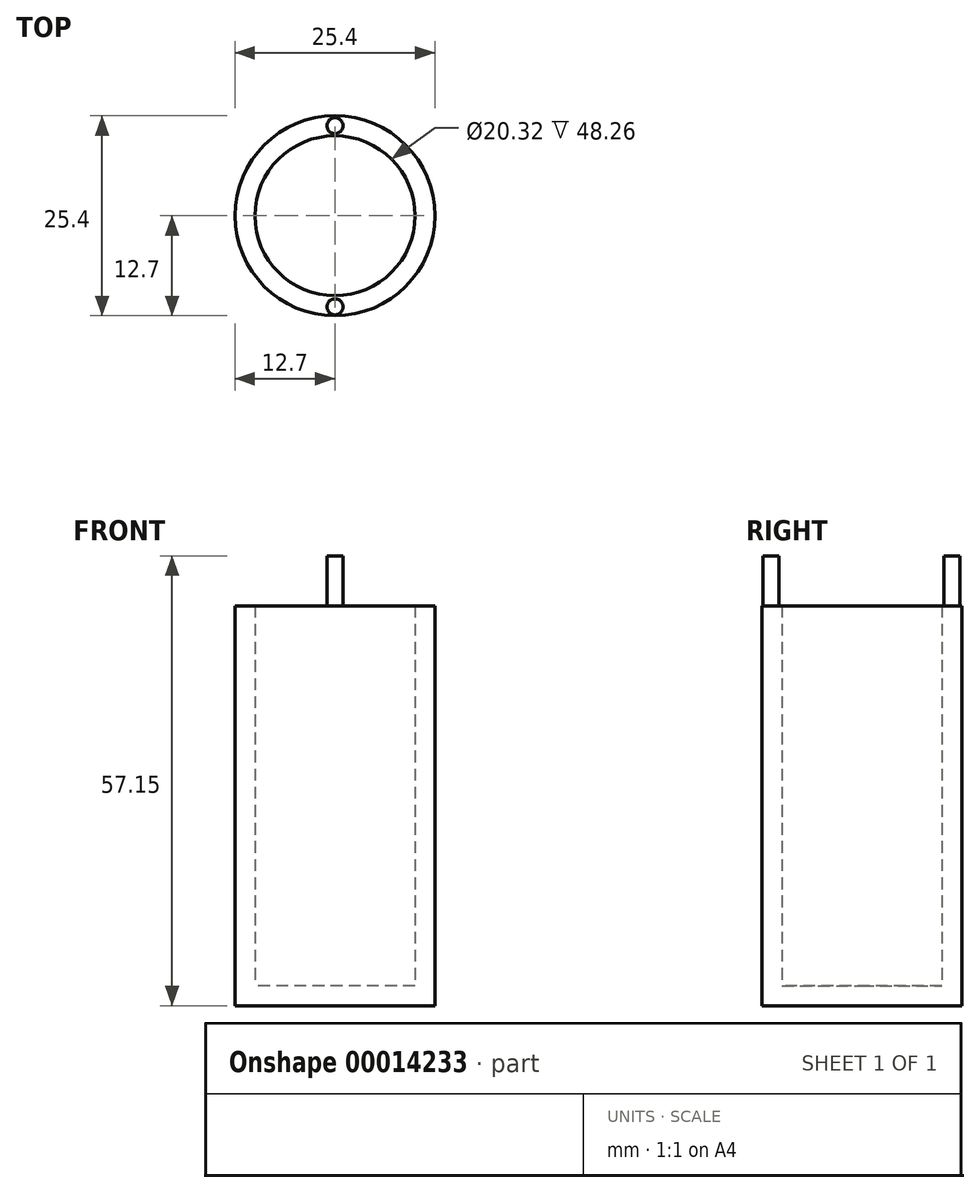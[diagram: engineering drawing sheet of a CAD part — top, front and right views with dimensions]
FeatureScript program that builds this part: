
annotation { "Feature Type Name" : "Feature", "Feature Type Description" : "" }
export const myFeature = defineFeature(function(context is Context, id is Id, definition is map)
    precondition{}
    {
        {
            var Q0;
            Q0=qCreatedBy(makeId("Top.planeOp"),FACE);
            var sketch = newSketch(context, id + "F0", { "sketchPlane" : qUnion([Q0])});
            skCircle(sketch, "E0", {"center": v(0, 0) * mm, "radius": 12.7 * mm});
            skSolve(sketch);
        }
        {
            var Q0;
            Q0=makeQuery(id+"F0.imprint","IMPRINT",FACE,{"disambiguationData":[TD([[makeQuery(id+"F0.imprint","IMPRINT",EDGE,{"derivedFrom":sQuery(id+"F0.wireOp",EDGE,"E0")}),1.0]])]});
            extrude(context, id + "F1", {"entities" : qUnion([Q0]), "depth" : 50.8 * mm});
        }
        {
            var Q0;
            Q0=makeQuery(id+"F1.opExtrude","CAP_FACE",FACE,{"disambiguationData":[OSD([sQuery(id+"F0.wireOp",EDGE,"E0")])],"isStart":false});
            shell(context, id + "F2", {"entities" : qUnion([Q0]), "thickness" : 2.54 * mm});
        }
        {
            var Q0;
            Q0=makeQuery(id+"F1.opExtrude","CAP_FACE",FACE,{"disambiguationData":[OSD([sQuery(id+"F0.wireOp",EDGE,"E0")])],"isStart":false});
            var sketch = newSketch(context, id + "F3", { "sketchPlane" : qUnion([Q0])});
            skCircle(sketch, "E1", {"center": v(0, -11.58) * mm, "radius": 1.02 * mm});
            skCircle(sketch, "E2", {"center": v(0, 11.44) * mm, "radius": 1.02 * mm});
            skSolve(sketch);
        }
        {
            var Q0;
            Q0=makeQuery(id+"F3.imprint","IMPRINT",FACE,{"disambiguationData":[TD([[makeQuery(id+"F3.imprint","IMPRINT",EDGE,{"derivedFrom":sQuery(id+"F3.wireOp",EDGE,"E1")}),1.0]])]});
            var Q1;
            Q1=makeQuery(id+"F3.imprint","IMPRINT",FACE,{"disambiguationData":[TD([[makeQuery(id+"F3.imprint","IMPRINT",EDGE,{"derivedFrom":sQuery(id+"F3.wireOp",EDGE,"E2")}),1.0]])]});
            extrude(context, id + "F4", {"entities" : qUnion([Q0, Q1]), "operationType" : NewBodyOperationType.ADD, "depth" : 6.35 * mm});
        }
    });
